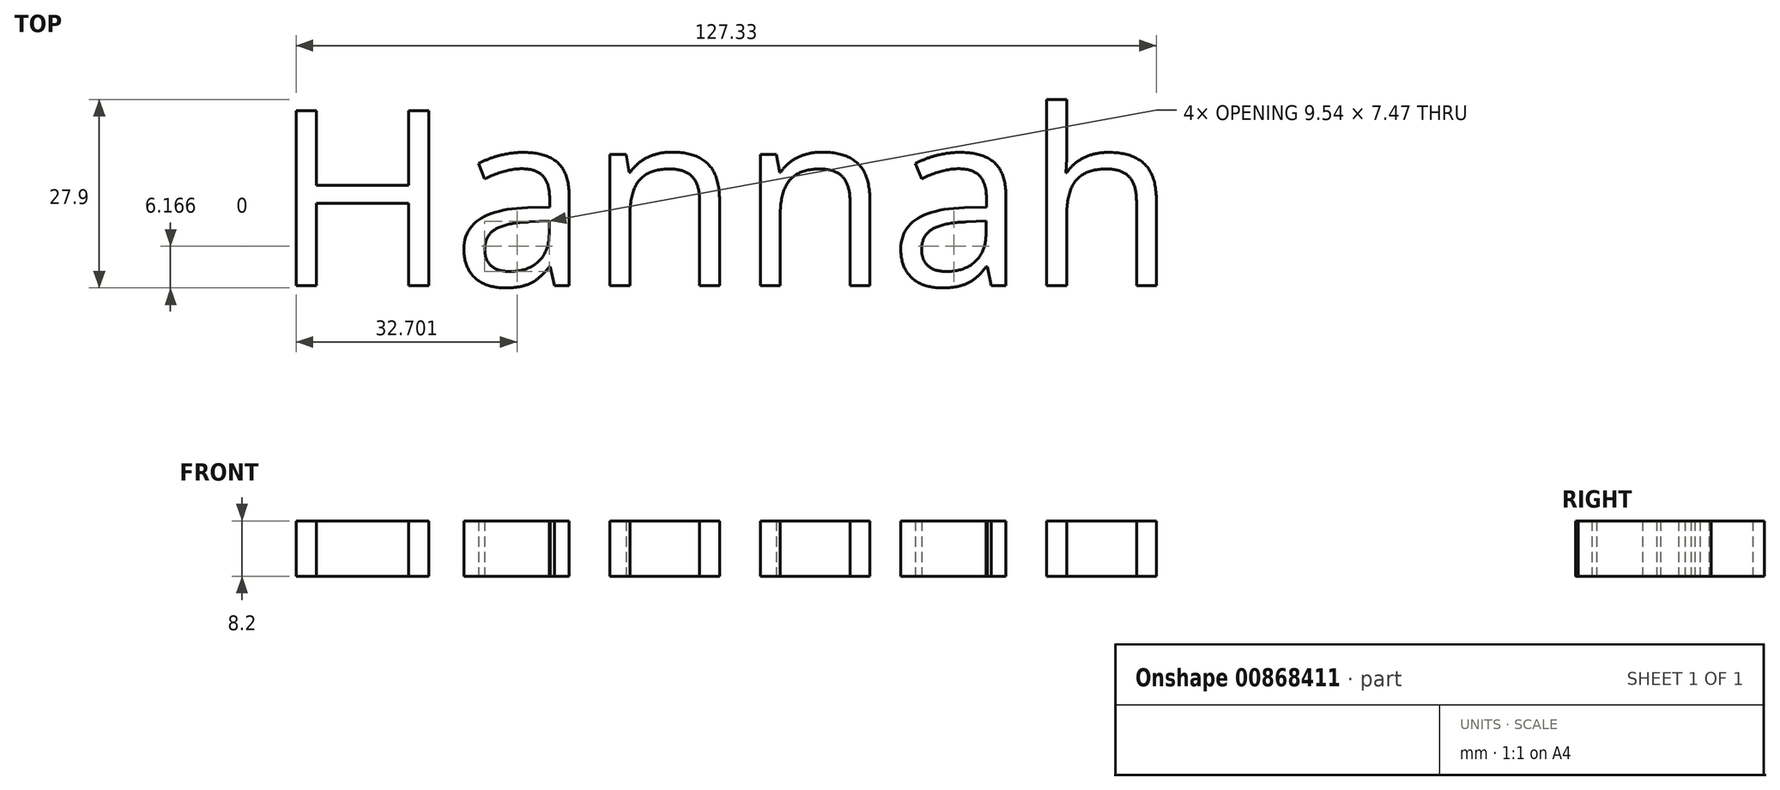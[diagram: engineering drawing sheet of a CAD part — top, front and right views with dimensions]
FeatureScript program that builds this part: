
annotation { "Feature Type Name" : "Feature", "Feature Type Description" : "" }
export const myFeature = defineFeature(function(context is Context, id is Id, definition is map)
    precondition{}
    {
        {
            var Q0;
            Q0=qCreatedBy(makeId("Top.planeOp"),FACE);
            var sketch = newSketch(context, id + "F0", { "sketchPlane" : qUnion([Q0])});
            skText(sketch, "E0", { "text": "Hannah", "fontName": "OpenSans-Regular.ttf"});
            const initialGuessF0  = {"E0": [-0.06772, 0.00818, 1, 0, 0.0261]};
            skSetInitialGuess(sketch, initialGuessF0);
            skSolve(sketch);
        }
        {
            var Q0;
            Q0 = qSketchRegion(id + "F0", true);
            extrude(context, id + "F1", {"entities" : qUnion([Q0]), "depth" : 8.2 * mm, "offsetDistance" : 25 * mm});
        }
    });
